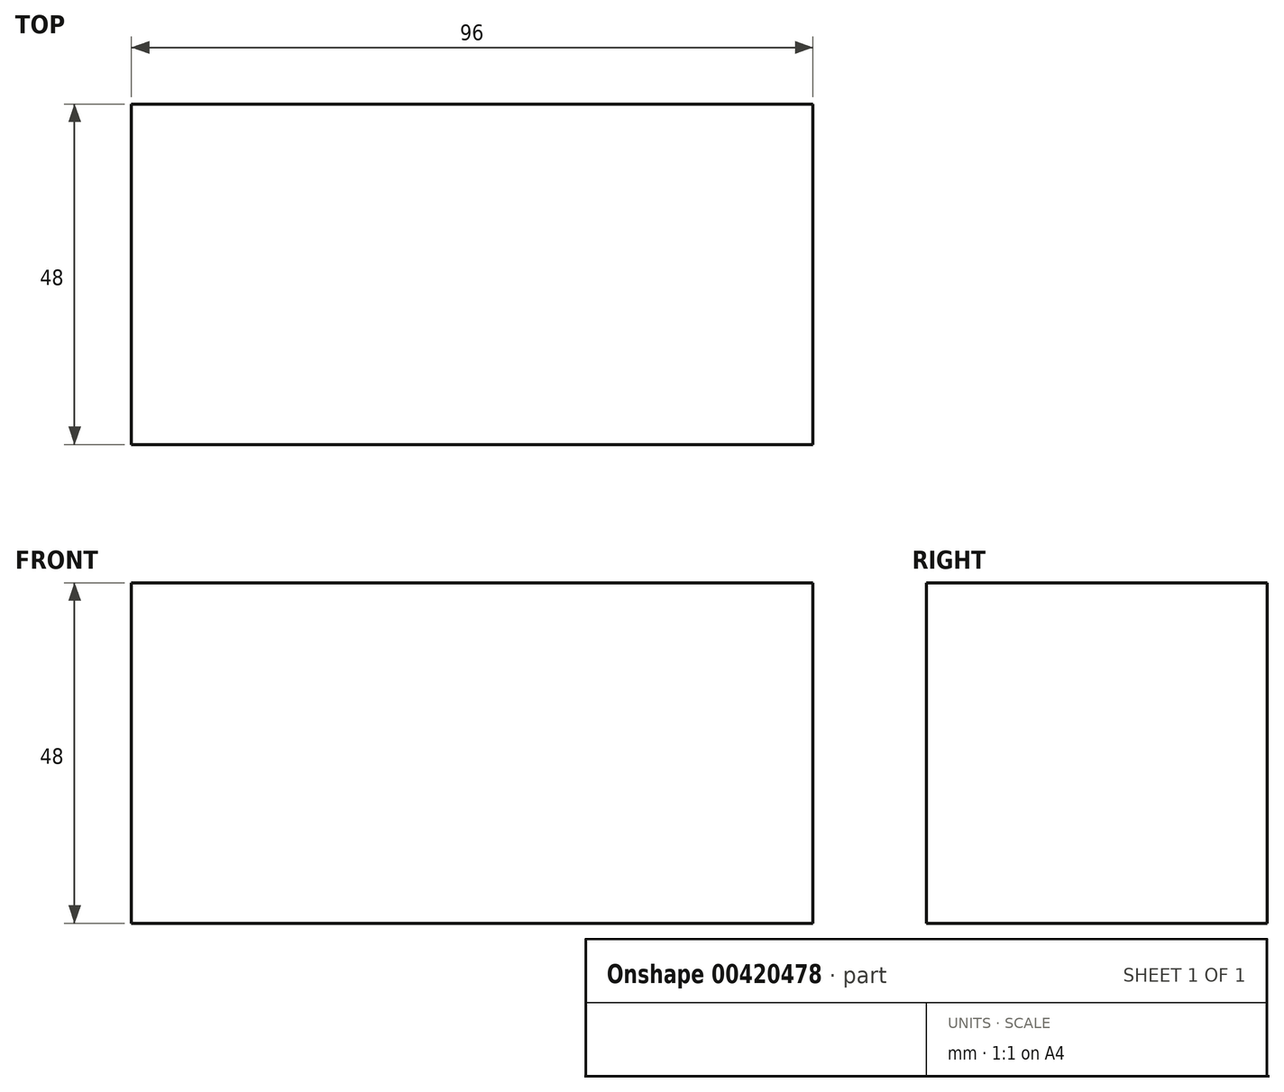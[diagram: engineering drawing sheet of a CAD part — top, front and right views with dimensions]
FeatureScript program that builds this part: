
annotation { "Feature Type Name" : "Feature", "Feature Type Description" : "" }
export const myFeature = defineFeature(function(context is Context, id is Id, definition is map)
    precondition{}
    {
        {
            var Q0;
            Q0=qCreatedBy(makeId("Front.planeOp"),FACE);
            var sketch = newSketch(context, id + "F0", { "sketchPlane" : qUnion([Q0])});
            skLineSegment(sketch, "E0.bottom", {"start": v(-48, 24) * mm, "end": v(48, 24) * mm});
            skLineSegment(sketch, "E0.top", {"start": v(-48, -24) * mm, "end": v(48, -24) * mm});
            skLineSegment(sketch, "E0.left", {"start": v(-48, 24) * mm, "end": v(-48, -24) * mm});
            skLineSegment(sketch, "E0.right", {"start": v(48, 24) * mm, "end": v(48, -24) * mm});
            skPoint(sketch, "E0.middle", {"position": v(0, 0) * mm});
            skSolve(sketch);
        }
        {
            var Q0;
            Q0=makeQuery(id+"F0.imprint","IMPRINT",FACE,{"disambiguationData":[TD([[makeQuery(id+"F0.imprint","IMPRINT",EDGE,{"derivedFrom":sQuery(id+"F0.wireOp",EDGE,"E0.bottom")}),-1.0]])]});
            extrude(context, id + "F1", {"entities" : qUnion([Q0]), "depth" : 48 * mm});
        }
    });
